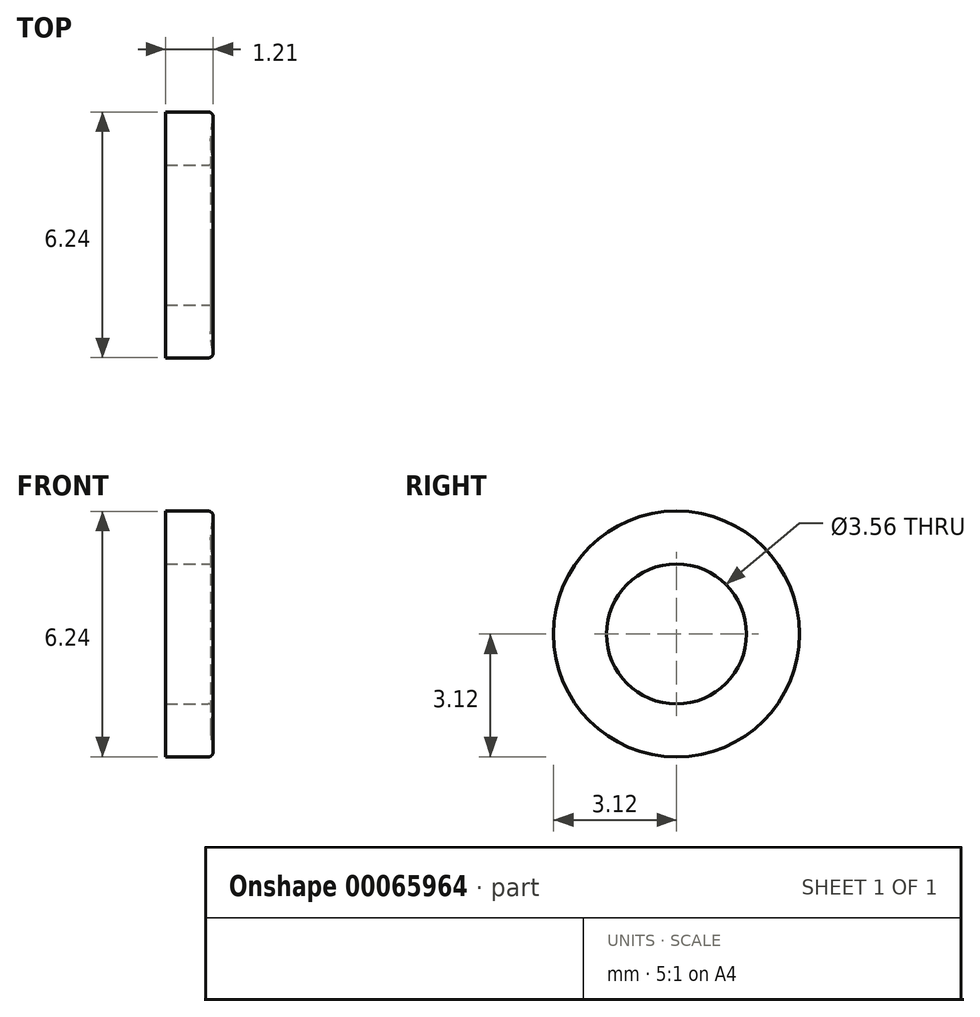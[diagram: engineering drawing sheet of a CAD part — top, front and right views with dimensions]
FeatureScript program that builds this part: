
annotation { "Feature Type Name" : "Feature", "Feature Type Description" : "" }
export const myFeature = defineFeature(function(context is Context, id is Id, definition is map)
    precondition{}
    {
        {
            var Q0;
            Q0=qCreatedBy(makeId("Front.planeOp"),FACE);
            var sketch = newSketch(context, id + "F0", { "sketchPlane" : qUnion([Q0])});
            skLineSegment(sketch, "E0.bottom", {"start": v(-0.17, 3.12) * mm, "end": v(-1.25, 3.12) * mm});
            skLineSegment(sketch, "E0.top", {"start": v(-0.17, 1.78) * mm, "end": v(-1.25, 1.78) * mm});
            skLineSegment(sketch, "E0.right", {"start": v(-1.25, 3.12) * mm, "end": v(-1.25, 1.78) * mm});
            skLineSegment(sketch, "E1", {"start": v(0, 0) * mm, "end": v(-6.16, 0) * mm, "construction": true});
            skArc(sketch, "E2", {"start": v(-0.04, 2.97) * mm, "mid": v(-0.1, 2.45) * mm, "end": v(-0.04, 1.93) * mm});
            skPoint(sketch, "E3.visualSharp", {"position": v(0, 3.12) * mm});
            skArc(sketch, "E3.filletArc", {"start": v(-0.04, 2.97) * mm, "mid": v(-0.07, 3.08) * mm, "end": v(-0.17, 3.12) * mm});
            skPoint(sketch, "E4.visualSharp", {"position": v(0, 1.78) * mm});
            skArc(sketch, "E4.filletArc", {"start": v(-0.17, 1.78) * mm, "mid": v(-0.07, 1.83) * mm, "end": v(-0.04, 1.93) * mm});
            skLineSegment(sketch, "E5", {"start": v(0, 1.78) * mm, "end": v(0, 0) * mm, "construction": true});
            skSolve(sketch);
        }
        {
            var Q0;
            Q0=makeQuery(id+"F0.imprint","IMPRINT",FACE,{"disambiguationData":[TD([[makeQuery(id+"F0.imprint","IMPRINT",EDGE,{"derivedFrom":sQuery(id+"F0.wireOp",EDGE,"E0.bottom")}),1.0]])]});
            var Q1;
            Q1=sQuery(id+"F0.wireOp",EDGE,"E1");
            revolve(context, id + "F1", {"entities" : qUnion([Q0]), "axis" : qUnion([Q1]), "revolveType" : RevolveType.FULL});
        }
    });
